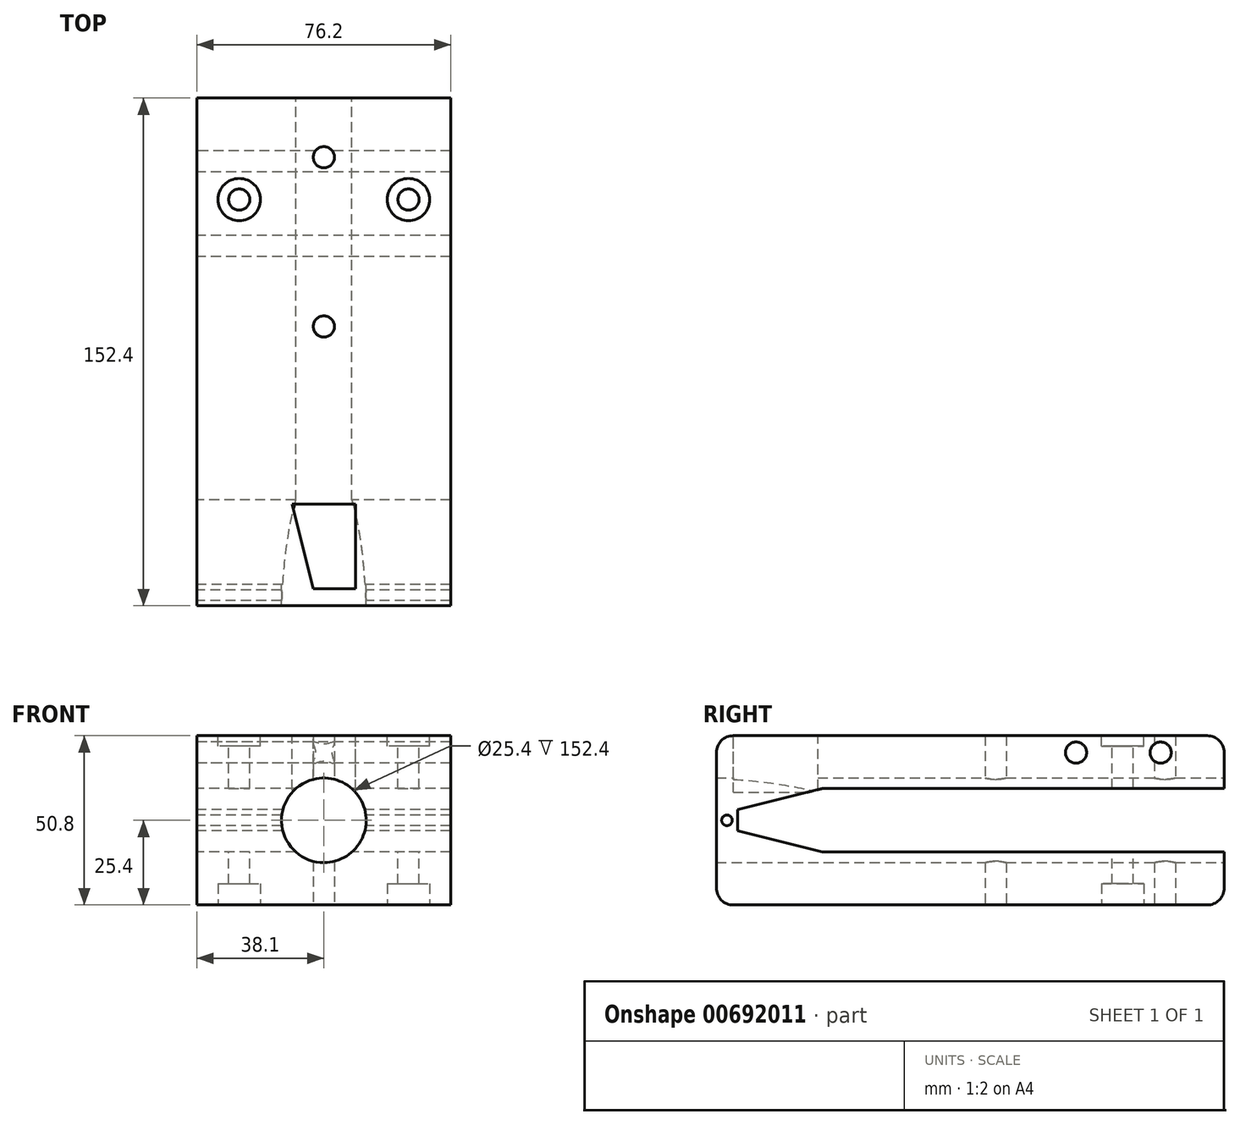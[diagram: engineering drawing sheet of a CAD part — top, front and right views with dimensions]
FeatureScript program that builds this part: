
annotation { "Feature Type Name" : "Feature", "Feature Type Description" : "" }
export const myFeature = defineFeature(function(context is Context, id is Id, definition is map)
    precondition{}
    {
        {
            var Q0;
            Q0=qCreatedBy(makeId("Front.planeOp"),FACE);
            var sketch = newSketch(context, id + "F0", { "sketchPlane" : qUnion([Q0])});
            skLineSegment(sketch, "E0.bottom", {"start": v(38.1, 25.4) * mm, "end": v(-38.1, 25.4) * mm});
            skLineSegment(sketch, "E0.top", {"start": v(38.1, -25.4) * mm, "end": v(-38.1, -25.4) * mm});
            skLineSegment(sketch, "E0.left", {"start": v(38.1, 25.4) * mm, "end": v(38.1, -25.4) * mm});
            skLineSegment(sketch, "E0.right", {"start": v(-38.1, 25.4) * mm, "end": v(-38.1, -25.4) * mm});
            skPoint(sketch, "E0.middle", {"position": v(0, 0) * mm});
            skCircle(sketch, "E1", {"center": v(0, 0) * mm, "radius": 12.7 * mm});
            skSolve(sketch);
        }
        {
            var Q0;
            Q0=makeQuery(id+"F0.imprint","IMPRINT",FACE,{"disambiguationData":[TD([[makeQuery(id+"F0.imprint","IMPRINT",EDGE,{"derivedFrom":sQuery(id+"F0.wireOp",EDGE,"E0.bottom")}),1.0]])]});
            extrude(context, id + "F1", {"entities" : qUnion([Q0]), "depth" : 152.4 * mm, "offsetDistance" : 25.4 * mm});
        }
        {
            var Q0;
            Q0=makeQuery(id+"F1.opExtrude","CAP_EDGE",EDGE,{"disambiguationData":[OSD([sQuery(id+"F0.wireOp",EDGE,"E0.bottom")])],"isStart":false});
            var Q1;
            Q1=makeQuery(id+"F1.opExtrude","CAP_EDGE",EDGE,{"disambiguationData":[OSD([sQuery(id+"F0.wireOp",EDGE,"E0.top")])],"isStart":false});
            var Q2;
            Q2=makeQuery(id+"F1.opExtrude","CAP_EDGE",EDGE,{"disambiguationData":[OSD([sQuery(id+"F0.wireOp",EDGE,"E0.bottom")])],"isStart":true});
            var Q3;
            Q3=makeQuery(id+"F1.opExtrude","CAP_EDGE",EDGE,{"disambiguationData":[OSD([sQuery(id+"F0.wireOp",EDGE,"E0.top")])],"isStart":true});
            fillet(context, id + "F2", {"entities" : qUnion([Q0, Q1, Q2, Q3]), "tangentPropagation" : true, "radius" : 5.08 * mm, "defaultsChanged" : false, "vertexSettings" : [], "allowEdgeOverflow" : false});
        }
        {
            var Q0;
            Q0=makeQuery(id+"F1.opExtrude","SWEPT_FACE",FACE,{"disambiguationData":[OSD([sQuery(id+"F0.wireOp",EDGE,"E0.right")])]});
            var sketch = newSketch(context, id + "F3", { "sketchPlane" : qUnion([Q0])});
            skLineSegment(sketch, "E2", {"start": v(0, 0) * mm, "end": v(12.7, 0) * mm});
            skLineSegment(sketch, "E3", {"start": v(12.7, 0) * mm, "end": v(139.7, 0) * mm});
            skLineSegment(sketch, "E4", {"start": v(139.7, 0) * mm, "end": v(88.9, 0) * mm});
            skLineSegment(sketch, "E5", {"start": v(88.9, 0) * mm, "end": v(88.9, 3.18) * mm});
            skLineSegment(sketch, "E6", {"start": v(88.9, 0) * mm, "end": v(88.9, -3.17) * mm});
            skLineSegment(sketch, "E7", {"start": v(0, -3.17) * mm, "end": v(0, 3.17) * mm});
            skLineSegment(sketch, "E8", {"start": v(139.7, 0) * mm, "end": v(146.05, 0) * mm});
            skLineSegment(sketch, "E9", {"start": v(146.05, 0) * mm, "end": v(146.05, 9.53) * mm});
            skLineSegment(sketch, "E10", {"start": v(146.05, 9.53) * mm, "end": v(146.05, -9.53) * mm});
            skLineSegment(sketch, "E11", {"start": v(146.05, -9.53) * mm, "end": v(0, -9.53) * mm});
            skLineSegment(sketch, "E12", {"start": v(0, -9.52) * mm, "end": v(0, 9.52) * mm});
            skLineSegment(sketch, "E13", {"start": v(0, 9.52) * mm, "end": v(146.05, 9.52) * mm});
            skLineSegment(sketch, "E14", {"start": v(146.05, 0) * mm, "end": v(146.05, 3.17) * mm});
            skLineSegment(sketch, "E15", {"start": v(146.05, 3.17) * mm, "end": v(146.05, -3.17) * mm});
            skLineSegment(sketch, "E16", {"start": v(146.05, -9.53) * mm, "end": v(120.65, -9.53) * mm});
            skLineSegment(sketch, "E17", {"start": v(120.65, -9.53) * mm, "end": v(120.65, 9.52) * mm});
            skLineSegment(sketch, "E18", {"start": v(120.65, -9.52) * mm, "end": v(146.05, -3.17) * mm});
            skLineSegment(sketch, "E19", {"start": v(120.65, 9.52) * mm, "end": v(146.05, 3.17) * mm});
            skLineSegment(sketch, "E20", {"start": v(146.05, 9.52) * mm, "end": v(0, 9.52) * mm});
            skSolve(sketch);
        }
        {
            var Q0;
            {var subQ5=sQuery(id+"F3.wireOp",EDGE,"E2");Q0=makeQuery(id+"F3.imprint","IMPRINT",FACE,{"disambiguationData":[TD([[makeQuery(id+"F3.imprint","IMPRINT",EDGE,{"derivedFrom":subQ5}),-1.0]])]});}
            var Q1;
            {var subQ1=sQuery(id+"F3.wireOp",EDGE,"E2");Q1=makeQuery(id+"F3.imprint","IMPRINT",FACE,{"disambiguationData":[TD([[makeQuery(id+"F3.imprint","IMPRINT",EDGE,{"derivedFrom":subQ1}),1.0]])]});}
            var Q2;
            {var subQ4=sQuery(id+"F3.wireOp",EDGE,"E8");Q2=makeQuery(id+"F3.imprint","IMPRINT",FACE,{"disambiguationData":[TD([[makeQuery(id+"F3.imprint","IMPRINT",EDGE,{"derivedFrom":subQ4}),1.0]])]});}
            var Q3;
            {var subQ4=sQuery(id+"F3.wireOp",EDGE,"E8");Q3=makeQuery(id+"F3.imprint","IMPRINT",FACE,{"disambiguationData":[TD([[makeQuery(id+"F3.imprint","IMPRINT",EDGE,{"derivedFrom":subQ4}),-1.0]])]});}
            extrude(context, id + "F4", {"entities" : qUnion([Q0, Q1, Q2, Q3]), "operationType" : NewBodyOperationType.REMOVE, "endBound" : BoundingType.THROUGH_ALL, "oppositeDirection" : true, "depth" : 25.4 * mm, "offsetDistance" : 25.4 * mm});
        }
        {
            var Q0;
            Q0=makeQuery(id+"F1.opExtrude","SWEPT_FACE",FACE,{"disambiguationData":[OSD([sQuery(id+"F0.wireOp",EDGE,"E0.bottom")])]});
            var sketch = newSketch(context, id + "F5", { "sketchPlane" : qUnion([Q0])});
            skLineSegment(sketch, "E21", {"start": v(0, -147.32) * mm, "end": v(9.53, -147.32) * mm});
            skLineSegment(sketch, "E22", {"start": v(9.52, -147.32) * mm, "end": v(-9.53, -147.32) * mm});
            skLineSegment(sketch, "E23", {"start": v(-9.53, -147.32) * mm, "end": v(-9.53, -5.08) * mm});
            skLineSegment(sketch, "E24", {"start": v(9.53, -147.32) * mm, "end": v(9.53, -5.08) * mm});
            skLineSegment(sketch, "E25", {"start": v(0, -147.32) * mm, "end": v(3.18, -147.32) * mm});
            skLineSegment(sketch, "E26", {"start": v(3.18, -147.32) * mm, "end": v(-3.17, -147.32) * mm});
            skLineSegment(sketch, "E27", {"start": v(9.53, -147.32) * mm, "end": v(9.53, -121.92) * mm});
            skLineSegment(sketch, "E28", {"start": v(9.53, -121.92) * mm, "end": v(-9.53, -121.92) * mm});
            skLineSegment(sketch, "E29", {"start": v(-9.53, -121.92) * mm, "end": v(-3.18, -147.32) * mm});
            skLineSegment(sketch, "E30", {"start": v(3.18, -147.32) * mm, "end": v(9.53, -121.92) * mm});
            skSolve(sketch);
        }
        {
            var Q0;
            Q0=makeQuery(id+"F5.imprint","IMPRINT",FACE,{"disambiguationData":[TD([[makeQuery(id+"F5.imprint","IMPRINT",EDGE,{"derivedFrom":sQuery(id+"F5.wireOp",EDGE,"E28")}),1.0]])]});
            var Q1;
            {var subQ5=sQuery(id+"F5.wireOp",EDGE,"E24");Q1=makeQuery(id+"F5.imprint","IMPRINT",FACE,{"disambiguationData":[TD([[makeQuery(id+"F5.imprint","IMPRINT",EDGE,{"derivedFrom":subQ5}),1.0]])]});}
            extrude(context, id + "F6", {"entities" : qUnion([Q0, Q1]), "operationType" : NewBodyOperationType.REMOVE, "oppositeDirection" : true, "depth" : 19.05 * mm, "offsetDistance" : 25.4 * mm});
        }
        {
            var Q0;
            Q0=makeQuery(id+"F1.opExtrude","SWEPT_FACE",FACE,{"disambiguationData":[OSD([sQuery(id+"F0.wireOp",EDGE,"E0.top")])]});
            var sketch = newSketch(context, id + "F7", { "sketchPlane" : qUnion([Q0])});
            skLineSegment(sketch, "E31", {"start": v(0, 5.08) * mm, "end": v(0, 147.32) * mm});
            skLineSegment(sketch, "E32", {"start": v(0, 5.08) * mm, "end": v(0, 17.78) * mm});
            skLineSegment(sketch, "E33", {"start": v(0, 17.78) * mm, "end": v(0, 43.18) * mm});
            skLineSegment(sketch, "E34", {"start": v(0, 43.18) * mm, "end": v(0, 68.58) * mm});
            skCircle(sketch, "E35", {"center": v(0, 68.58) * mm, "radius": 3.18 * mm});
            skCircle(sketch, "E36", {"center": v(0, 17.78) * mm, "radius": 3.18 * mm});
            skSolve(sketch);
        }
        {
            var Q0;
            Q0 = qSketchRegion(id + "F7", true);
            extrude(context, id + "F8", {"entities" : qUnion([Q0]), "operationType" : NewBodyOperationType.REMOVE, "endBound" : BoundingType.THROUGH_ALL, "oppositeDirection" : true, "depth" : 25.4 * mm, "offsetDistance" : 25.4 * mm});
        }
        {
            var Q0;
            Q0=makeQuery(id+"F1.opExtrude","SWEPT_FACE",FACE,{"disambiguationData":[OSD([sQuery(id+"F0.wireOp",EDGE,"E0.right")])]});
            var sketch = newSketch(context, id + "F9", { "sketchPlane" : qUnion([Q0])});
            skLineSegment(sketch, "E37", {"start": v(152.4, 0) * mm, "end": v(146.05, 0) * mm});
            skLineSegment(sketch, "E38", {"start": v(146.05, 0) * mm, "end": v(149.22, 0) * mm});
            skCircle(sketch, "E39", {"center": v(149.22, 0) * mm, "radius": 1.59 * mm});
            skSolve(sketch);
        }
        {
            var Q0;
            {var subQ0=sQuery(id+"F9.wireOp",EDGE,"E37");var subQ1=makeQuery(id+"F9.imprint","IMPRINT",VERTEX,{"derivedFrom":subQ0});var subQ4=makeQuery(id+"F9.imprint","IMPRINT",EDGE,{"disambiguationData":[TD([[subQ1,1.0]])],"derivedFrom":subQ0});Q0=qUnion([makeQuery(id+"F9.imprint","IMPRINT",FACE,{"disambiguationData":[TD([[subQ4,1.0]])]}),makeQuery(id+"F9.imprint","IMPRINT",FACE,{"disambiguationData":[TD([[subQ4,-1.0]])]})]);}
            extrude(context, id + "F10", {"entities" : qUnion([Q0]), "operationType" : NewBodyOperationType.REMOVE, "endBound" : BoundingType.THROUGH_ALL, "oppositeDirection" : true, "depth" : 25.4 * mm, "offsetDistance" : 25.4 * mm});
        }
        {
            var Q0;
            {var subQ0=sQuery(id+"F0.wireOp",EDGE,"E0.bottom");Q0=makeQuery(id+"F6.boolean.opBoolean","SPLIT",FACE,{"disambiguationData":[TD([makeQuery(id+"F1.opExtrude","SWEPT_FACE",FACE,{"disambiguationData":[OSD([sQuery(id+"F0.wireOp",EDGE,"E0.right")])]})])],"derivedFrom":makeQuery(id+"F1.opExtrude","SWEPT_FACE",FACE,{"disambiguationData":[OSD([subQ0])]})});}
            var sketch = newSketch(context, id + "F11", { "sketchPlane" : qUnion([Q0])});
            skLineSegment(sketch, "E40", {"start": v(0, 0) * mm, "end": v(0, -5.08) * mm});
            skLineSegment(sketch, "E41", {"start": v(0, -5.08) * mm, "end": v(-25.4, -5.08) * mm});
            skLineSegment(sketch, "E42", {"start": v(-25.4, -5.08) * mm, "end": v(-25.4, -30.48) * mm});
            skLineSegment(sketch, "E43", {"start": v(0, -5.08) * mm, "end": v(25.4, -5.08) * mm});
            skLineSegment(sketch, "E44", {"start": v(25.4, -5.08) * mm, "end": v(25.4, -30.48) * mm});
            skCircle(sketch, "E45", {"center": v(-25.4, -30.48) * mm, "radius": 6.35 * mm});
            skCircle(sketch, "E46", {"center": v(25.4, -30.48) * mm, "radius": 6.35 * mm});
            skSolve(sketch);
        }
        {
            var Q0;
            Q0 = qSketchRegion(id + "F11", true);
            extrude(context, id + "F12", {"entities" : qUnion([Q0]), "operationType" : NewBodyOperationType.REMOVE, "oppositeDirection" : true, "depth" : 3.17 * mm, "offsetDistance" : 25.4 * mm});
        }
        {
            var Q0;
            Q0=makeQuery(id+"F12.boolean.opBoolean","COPY",FACE,{"derivedFrom":makeQuery(id+"F12.opExtrude","CAP_FACE",FACE,{"disambiguationData":[OSD([sQuery(id+"F11.wireOp",EDGE,"E46")])],"isStart":false})});
            var sketch = newSketch(context, id + "F13", { "sketchPlane" : qUnion([Q0])});
            skCircle(sketch, "E47", {"center": v(25.4, -30.48) * mm, "radius": 3.18 * mm});
            skSolve(sketch);
        }
        {
            var Q0;
            Q0 = qSketchRegion(id + "F13", true);
            extrude(context, id + "F14", {"entities" : qUnion([Q0]), "operationType" : NewBodyOperationType.REMOVE, "endBound" : BoundingType.THROUGH_ALL, "oppositeDirection" : true, "depth" : 25.4 * mm, "offsetDistance" : 25.4 * mm});
        }
        {
            var Q0;
            Q0=makeQuery(id+"F12.boolean.opBoolean","COPY",FACE,{"derivedFrom":makeQuery(id+"F12.opExtrude","CAP_FACE",FACE,{"disambiguationData":[OSD([sQuery(id+"F11.wireOp",EDGE,"E45")])],"isStart":false})});
            var sketch = newSketch(context, id + "F15", { "sketchPlane" : qUnion([Q0])});
            skCircle(sketch, "E48", {"center": v(-25.4, -30.48) * mm, "radius": 3.18 * mm});
            skSolve(sketch);
        }
        {
            var Q0;
            Q0 = qSketchRegion(id + "F15", true);
            extrude(context, id + "F16", {"entities" : qUnion([Q0]), "operationType" : NewBodyOperationType.REMOVE, "endBound" : BoundingType.THROUGH_ALL, "oppositeDirection" : true, "depth" : 25.4 * mm, "offsetDistance" : 25.4 * mm});
        }
        {
            var Q0;
            Q0=makeQuery(id+"F1.opExtrude","SWEPT_FACE",FACE,{"disambiguationData":[OSD([sQuery(id+"F0.wireOp",EDGE,"E0.top")])]});
            var sketch = newSketch(context, id + "F17", { "sketchPlane" : qUnion([Q0])});
            skCircle(sketch, "E49", {"center": v(-25.4, 30.48) * mm, "radius": 6.35 * mm});
            skCircle(sketch, "E50", {"center": v(25.4, 30.48) * mm, "radius": 6.35 * mm});
            skSolve(sketch);
        }
        {
            var Q0;
            Q0 = qSketchRegion(id + "F17", true);
            extrude(context, id + "F18", {"entities" : qUnion([Q0]), "operationType" : NewBodyOperationType.REMOVE, "oppositeDirection" : true, "depth" : 6.35 * mm, "offsetDistance" : 25.4 * mm});
        }
        {
            var Q0;
            Q0=makeQuery(id+"F1.opExtrude","SWEPT_FACE",FACE,{"disambiguationData":[OSD([sQuery(id+"F0.wireOp",EDGE,"E0.right")])]});
            var sketch = newSketch(context, id + "F19", { "sketchPlane" : qUnion([Q0])});
            skLineSegment(sketch, "E51", {"start": v(19.05, 20.32) * mm, "end": v(44.45, 20.32) * mm});
            skCircle(sketch, "E52", {"center": v(19.05, 20.32) * mm, "radius": 3.18 * mm});
            skCircle(sketch, "E53", {"center": v(44.45, 20.32) * mm, "radius": 3.18 * mm});
            skLineSegment(sketch, "E54", {"start": v(6.15, 9.52) * mm, "end": v(6.15, 25.4) * mm});
            skSolve(sketch);
        }
        {
            var Q0;
            Q0 = qSketchRegion(id + "F19", true);
            extrude(context, id + "F20", {"entities" : qUnion([Q0]), "operationType" : NewBodyOperationType.REMOVE, "endBound" : BoundingType.THROUGH_ALL, "oppositeDirection" : true, "depth" : 25.4 * mm, "offsetDistance" : 25.4 * mm});
        }
    });
